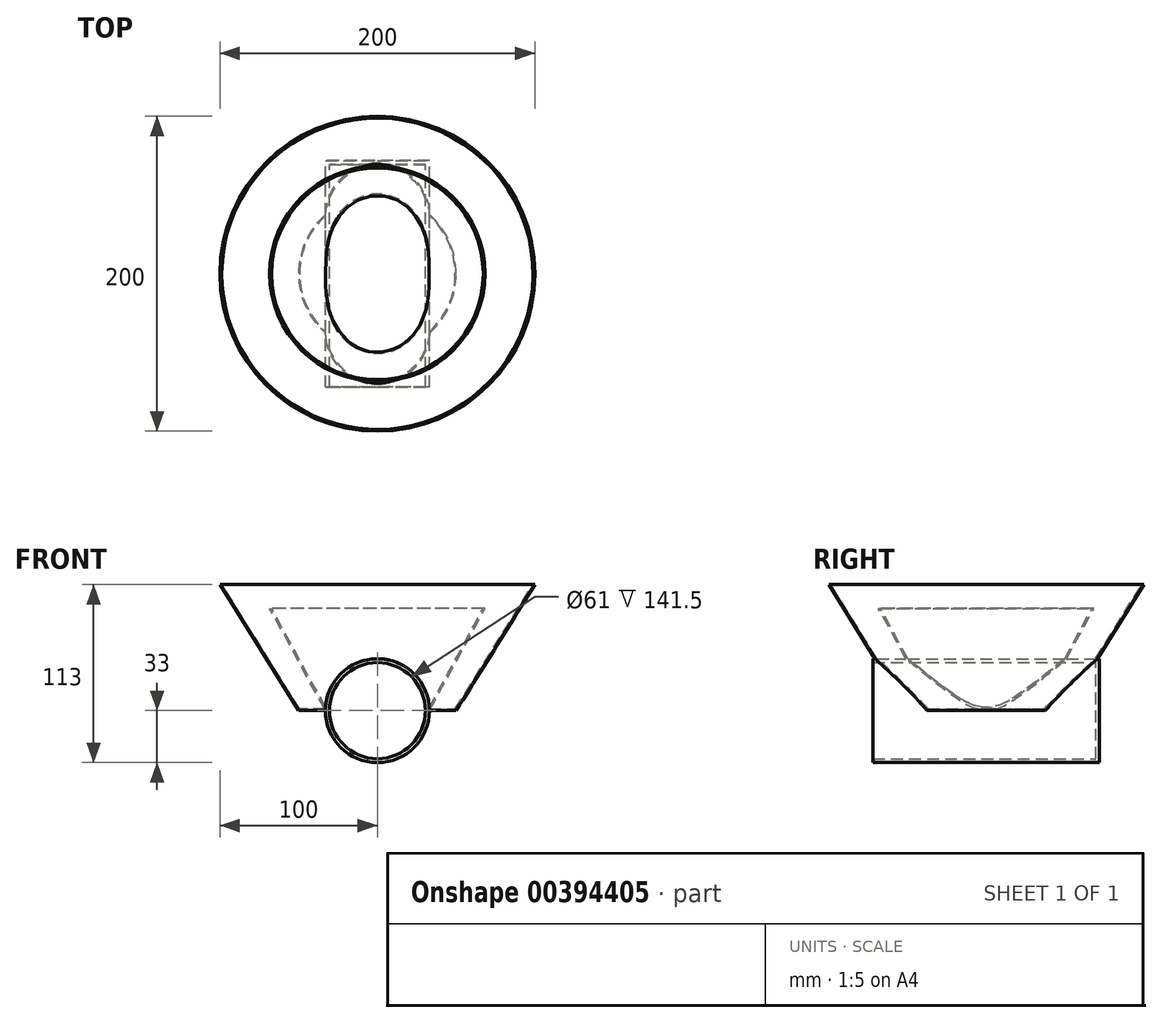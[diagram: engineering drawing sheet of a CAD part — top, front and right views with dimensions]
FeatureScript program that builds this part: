
annotation { "Feature Type Name" : "Feature", "Feature Type Description" : "" }
export const myFeature = defineFeature(function(context is Context, id is Id, definition is map)
    precondition{}
    {
        {
            var Q0;
            Q0=qCreatedBy(makeId("Right.planeOp"),FACE);
            var sketch = newSketch(context, id + "F0", { "sketchPlane" : qUnion([Q0])});
            skLineSegment(sketch, "E0", {"start": v(0, 0) * mm, "end": v(50, 0) * mm});
            skLineSegment(sketch, "E1", {"start": v(50, 0) * mm, "end": v(100, 80) * mm});
            skLineSegment(sketch, "E2", {"start": v(100, 80) * mm, "end": v(0, 80) * mm});
            skLineSegment(sketch, "E3", {"start": v(0, 80) * mm, "end": v(0, 0) * mm});
            skCircle(sketch, "E4", {"center": v(0, 0) * mm, "radius": 33 * mm});
            skLineSegment(sketch, "E5", {"start": v(0, 65) * mm, "end": v(68.38, 65) * mm});
            skLineSegment(sketch, "E6", {"start": v(33, 0) * mm, "end": v(68.38, 65) * mm});
            skLineSegment(sketch, "E7", {"start": v(68.38, 65) * mm, "end": v(100, 80) * mm});
            skSolve(sketch);
        }
        {
            var Q0;
            Q0=qCreatedBy(makeId("Front.planeOp"),FACE);
            var sketch = newSketch(context, id + "F1", { "sketchPlane" : qUnion([Q0])});
            skLineSegment(sketch, "E8.bottom", {"start": v(-117.9, 50) * mm, "end": v(132.1, 50) * mm});
            skLineSegment(sketch, "E8.top", {"start": v(-117.9, 80) * mm, "end": v(132.1, 80) * mm});
            skLineSegment(sketch, "E8.left", {"start": v(-117.9, 50) * mm, "end": v(-117.9, 80) * mm});
            skLineSegment(sketch, "E8.right", {"start": v(132.1, 50) * mm, "end": v(132.1, 80) * mm});
            skCircle(sketch, "E9", {"center": v(0, 0) * mm, "radius": 33 * mm});
            skLineSegment(sketch, "E10", {"start": v(-86.34, -100) * mm, "end": v(105.64, -100) * mm});
            skLineSegment(sketch, "E11", {"start": v(0, 80) * mm, "end": v(74.64, 80) * mm});
            skSolve(sketch);
        }
        {
            var Q0;
            {var subQ0=sQuery(id+"F0.wireOp",EDGE,"E1");Q0=makeQuery(id+"F0.imprint","IMPRINT",FACE,{"disambiguationData":[TD([[makeQuery(id+"F0.imprint","IMPRINT",EDGE,{"derivedFrom":subQ0}),1.0]])]});}
            var Q1;
            {var subQ0=sQuery(id+"F0.wireOp",EDGE,"E2");Q1=makeQuery(id+"F0.imprint","IMPRINT",FACE,{"disambiguationData":[TD([[makeQuery(id+"F0.imprint","IMPRINT",EDGE,{"derivedFrom":subQ0}),1.0]])]});}
            var Q2;
            {var subQ0=sQuery(id+"F0.wireOp",EDGE,"E5");Q2=makeQuery(id+"F0.imprint","IMPRINT",FACE,{"disambiguationData":[TD([[makeQuery(id+"F0.imprint","IMPRINT",EDGE,{"derivedFrom":subQ0}),-1.0]])]});}
            var Q3;
            {var subQ0=sQuery(id+"F0.wireOp",EDGE,"E3");var subQ1=sQuery(id+"F0.wireOp",EDGE,"E0");var subQ2=makeQuery(id+"F0.imprint","INTERSECT",VERTEX,{"derivedFrom":[subQ1,subQ0]});Q3=makeQuery(id+"F0.imprint","IMPRINT",FACE,{"disambiguationData":[TD([[makeQuery(id+"F0.imprint","IMPRINT",EDGE,{"disambiguationData":[TD([[subQ2,1.0]])],"derivedFrom":subQ0}),1.0]])]});}
            var Q4;
            Q4=sQuery(id+"F0.wireOp",EDGE,"E3");
            revolve(context, id + "F2", {"surfaceOperationType" : NewSurfaceOperationType.NEW, "entities" : qUnion([Q0, Q1, Q2, Q3]), "axis" : qUnion([Q4]), "revolveType" : RevolveType.FULL});
        }
        {
            var Q0;
            Q0=makeQuery(id+"F2.opRevolve","SWEPT_FACE",FACE,{"disambiguationData":[OSD([sQuery(id+"F0.wireOp",EDGE,"E2")])]});
            shell(context, id + "F3", {"entities" : qUnion([Q0]), "thickness" : 1 * mm});
        }
        {
            var Q0;
            {var subQ0=sQuery(id+"F0.wireOp",EDGE,"E5");Q0=makeQuery(id+"F0.imprint","IMPRINT",FACE,{"disambiguationData":[TD([[makeQuery(id+"F0.imprint","IMPRINT",EDGE,{"derivedFrom":subQ0}),-1.0]])]});}
            var Q1;
            {var subQ0=sQuery(id+"F0.wireOp",EDGE,"E3");var subQ1=sQuery(id+"F0.wireOp",EDGE,"E0");var subQ2=makeQuery(id+"F0.imprint","INTERSECT",VERTEX,{"derivedFrom":[subQ1,subQ0]});Q1=makeQuery(id+"F0.imprint","IMPRINT",FACE,{"disambiguationData":[TD([[makeQuery(id+"F0.imprint","IMPRINT",EDGE,{"disambiguationData":[TD([[subQ2,1.0]])],"derivedFrom":subQ0}),1.0]])]});}
            var Q2;
            Q2=sQuery(id+"F0.wireOp",EDGE,"E3");
            revolve(context, id + "F4", {"operationType" : NewBodyOperationType.ADD, "entities" : qUnion([Q0, Q1]), "axis" : qUnion([Q2]), "revolveType" : RevolveType.FULL});
        }
        {
            var Q0;
            Q0=makeQuery(id+"F4.opRevolve","SWEPT_FACE",FACE,{"disambiguationData":[OSD([sQuery(id+"F0.wireOp",EDGE,"E5")])]});
            shell(context, id + "F5", {"entities" : qUnion([Q0]), "thickness" : 1 * mm});
        }
        {
            var Q0;
            Q0=makeQuery(id+"F1.imprint","IMPRINT",FACE,{"disambiguationData":[TD([[makeQuery(id+"F1.imprint","IMPRINT",EDGE,{"derivedFrom":sQuery(id+"F1.wireOp",EDGE,"E9")}),1.0]])]});
            extrude(context, id + "F6", {"entities" : qUnion([Q0]), "operationType" : NewBodyOperationType.ADD, "endBound" : BoundingType.SYMMETRIC, "depth" : 144 * mm});
        }
        {
            var Q0;
            Q0=makeQuery(id+"F6.opExtrude","CAP_FACE",FACE,{"disambiguationData":[OSD([sQuery(id+"F1.wireOp",EDGE,"E9")])],"isStart":false});
            shell(context, id + "F7", {"entities" : qUnion([Q0]), "thickness" : 2.5 * mm});
        }
    });
